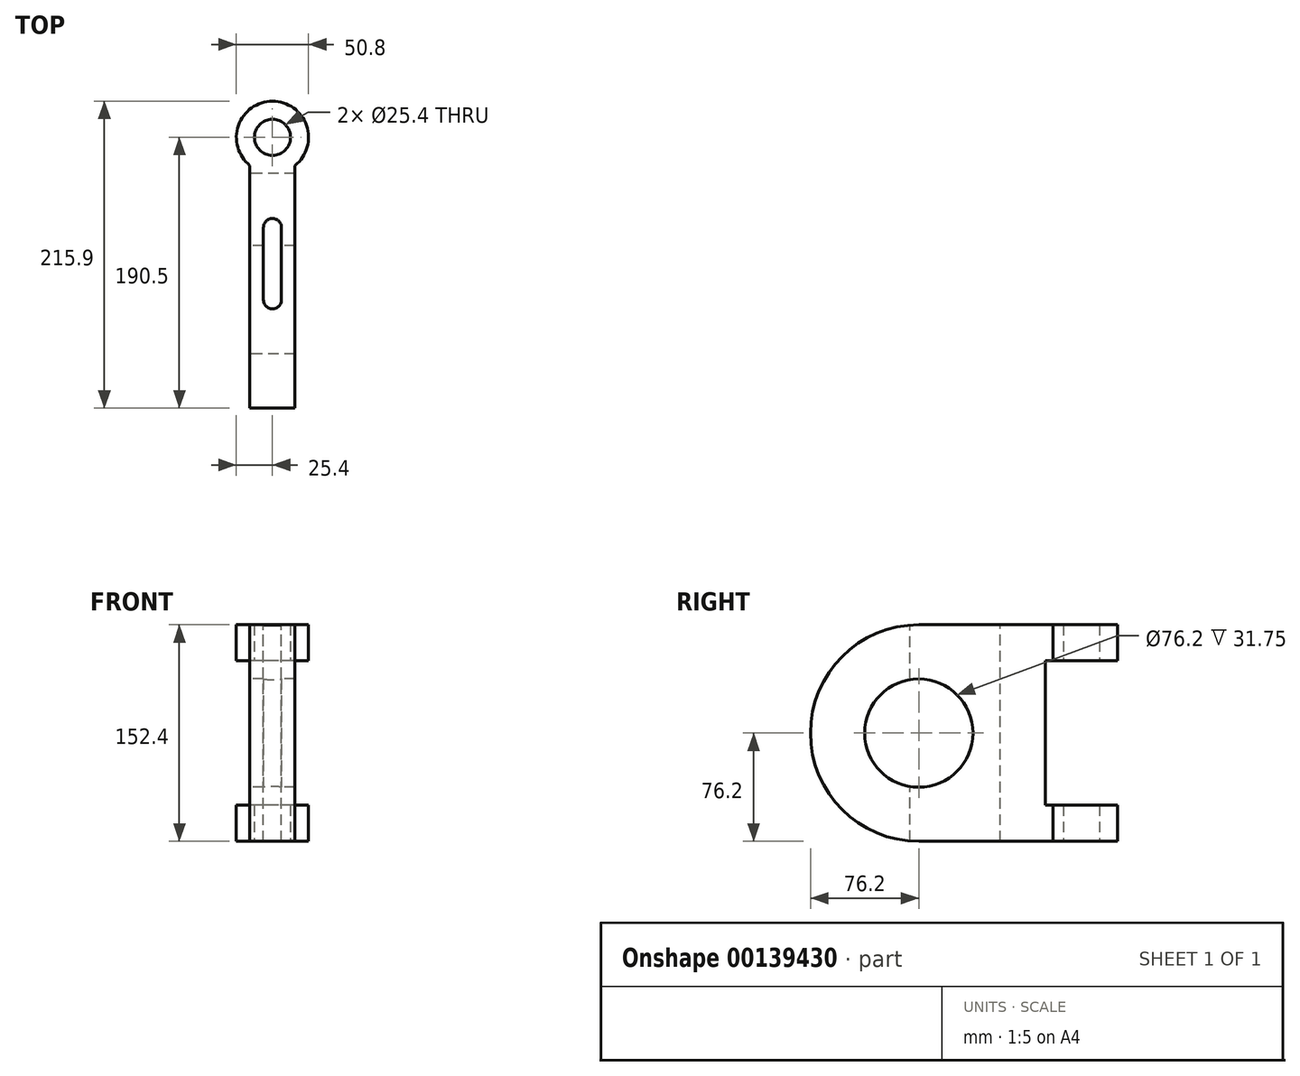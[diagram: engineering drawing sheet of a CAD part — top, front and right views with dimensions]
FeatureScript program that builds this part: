
annotation { "Feature Type Name" : "Feature", "Feature Type Description" : "" }
export const myFeature = defineFeature(function(context is Context, id is Id, definition is map)
    precondition{}
    {
        {
            var Q0;
            Q0=qCreatedBy(makeId("Top.planeOp"),FACE);
            var sketch = newSketch(context, id + "F0", { "sketchPlane" : qUnion([Q0])});
            skCircle(sketch, "E0", {"center": v(0, 0) * mm, "radius": 12.7 * mm});
            skArc(sketch, "E1", {"start": v(15.88, -19.83) * mm, "mid": v(0, 25.4) * mm, "end": v(-15.88, -19.83) * mm});
            skLineSegment(sketch, "E2", {"start": v(-15.88, -19.83) * mm, "end": v(-15.87, -190.5) * mm});
            skLineSegment(sketch, "E3", {"start": v(15.87, -19.83) * mm, "end": v(15.88, -190.5) * mm});
            skLineSegment(sketch, "E4", {"start": v(-15.87, -190.5) * mm, "end": v(15.87, -190.5) * mm});
            skSolve(sketch);
        }
        {
            var Q0;
            Q0=makeQuery(id+"F0.imprint","IMPRINT",FACE,{"disambiguationData":[TD([[makeQuery(id+"F0.imprint","IMPRINT",EDGE,{"derivedFrom":sQuery(id+"F0.wireOp",EDGE,"E0")}),-1.0]])]});
            extrude(context, id + "F1", {"entities" : qUnion([Q0]), "depth" : 152.4 * mm});
        }
        {
            var Q0;
            Q0=makeQuery(id+"F1.opExtrude","CAP_EDGE",EDGE,{"disambiguationData":[OSD([sQuery(id+"F0.wireOp",EDGE,"E4")])],"isStart":false});
            var Q1;
            Q1=makeQuery(id+"F1.opExtrude","CAP_EDGE",EDGE,{"disambiguationData":[OSD([sQuery(id+"F0.wireOp",EDGE,"E4")])],"isStart":true});
            fillet(context, id + "F2", {"entities" : qUnion([Q0, Q1]), "radius" : 76.2 * mm, "tangentPropagation" : true, "allowEdgeOverflow" : false});
        }
        {
            var Q0;
            Q0=makeQuery(id+"F1.opExtrude","SWEPT_FACE",FACE,{"disambiguationData":[OSD([sQuery(id+"F0.wireOp",EDGE,"E2")])]});
            var sketch = newSketch(context, id + "F3", { "sketchPlane" : qUnion([Q0])});
            skCircle(sketch, "E5", {"center": v(114.3, 76.2) * mm, "radius": 38.1 * mm});
            skPoint(sketch, "E6.orphan", {"position": v(114.3, 152.4) * mm});
            skPoint(sketch, "E7.end.orphan", {"position": v(114.3, 0) * mm});
            skLineSegment(sketch, "E8.bottom", {"start": v(25.4, 127) * mm, "end": v(-53.38, 127) * mm});
            skLineSegment(sketch, "E8.top", {"start": v(25.4, 25.4) * mm, "end": v(-53.38, 25.4) * mm});
            skLineSegment(sketch, "E8.left", {"start": v(25.4, 127) * mm, "end": v(25.4, 25.4) * mm});
            skLineSegment(sketch, "E8.right", {"start": v(-53.38, 127) * mm, "end": v(-53.38, 25.4) * mm});
            skSolve(sketch);
        }
        {
            var Q0;
            Q0 = qSketchRegion(id + "F3", true);
            extrude(context, id + "F4", {"entities" : qUnion([Q0]), "operationType" : NewBodyOperationType.REMOVE, "endBound" : BoundingType.SYMMETRIC, "oppositeDirection" : true, "depth" : 5892.8 * mm});
        }
        {
            var Q0;
            Q0=makeQuery(id+"F1.opExtrude","CAP_FACE",FACE,{"disambiguationData":[OSD([sQuery(id+"F0.wireOp",EDGE,"E0"),sQuery(id+"F0.wireOp",EDGE,"E1"),sQuery(id+"F0.wireOp",EDGE,"E2"),sQuery(id+"F0.wireOp",EDGE,"E3"),sQuery(id+"F0.wireOp",EDGE,"E4")])],"isStart":false});
            var sketch = newSketch(context, id + "F5", { "sketchPlane" : qUnion([Q0])});
            skArc(sketch, "E9", {"start": v(6.35, -63.5) * mm, "mid": v(0, -57.15) * mm, "end": v(-6.35, -63.5) * mm});
            skPoint(sketch, "E10.center.orphan", {"position": v(0, -127) * mm});
            skLineSegment(sketch, "E11", {"start": v(-6.35, -63.5) * mm, "end": v(-6.35, -114.3) * mm});
            skLineSegment(sketch, "E12", {"start": v(6.35, -63.5) * mm, "end": v(6.35, -114.3) * mm});
            skArc(sketch, "E13", {"start": v(-6.35, -114.3) * mm, "mid": v(0, -120.65) * mm, "end": v(6.35, -114.3) * mm});
            skSolve(sketch);
        }
        {
            var Q0;
            Q0 = qSketchRegion(id + "F5", true);
            var Q1;
            {var subQ0=sQuery(id+"F5.wireOp",EDGE,"zWkzQtGs-OlHw-nKsV-bn0d-CN7leWMA8WgE");Q1=makeQuery(id+"F5.imprint","IMPRINT",FACE,{"disambiguationData":[TD([[makeQuery(id+"F5.imprint","IMPRINT",EDGE,{"derivedFrom":subQ0}),-1.0]])]});}
            extrude(context, id + "F6", {"entities" : qUnion([Q0, Q1]), "operationType" : NewBodyOperationType.REMOVE, "oppositeDirection" : true, "depth" : 178.3 * mm});
        }
    });
